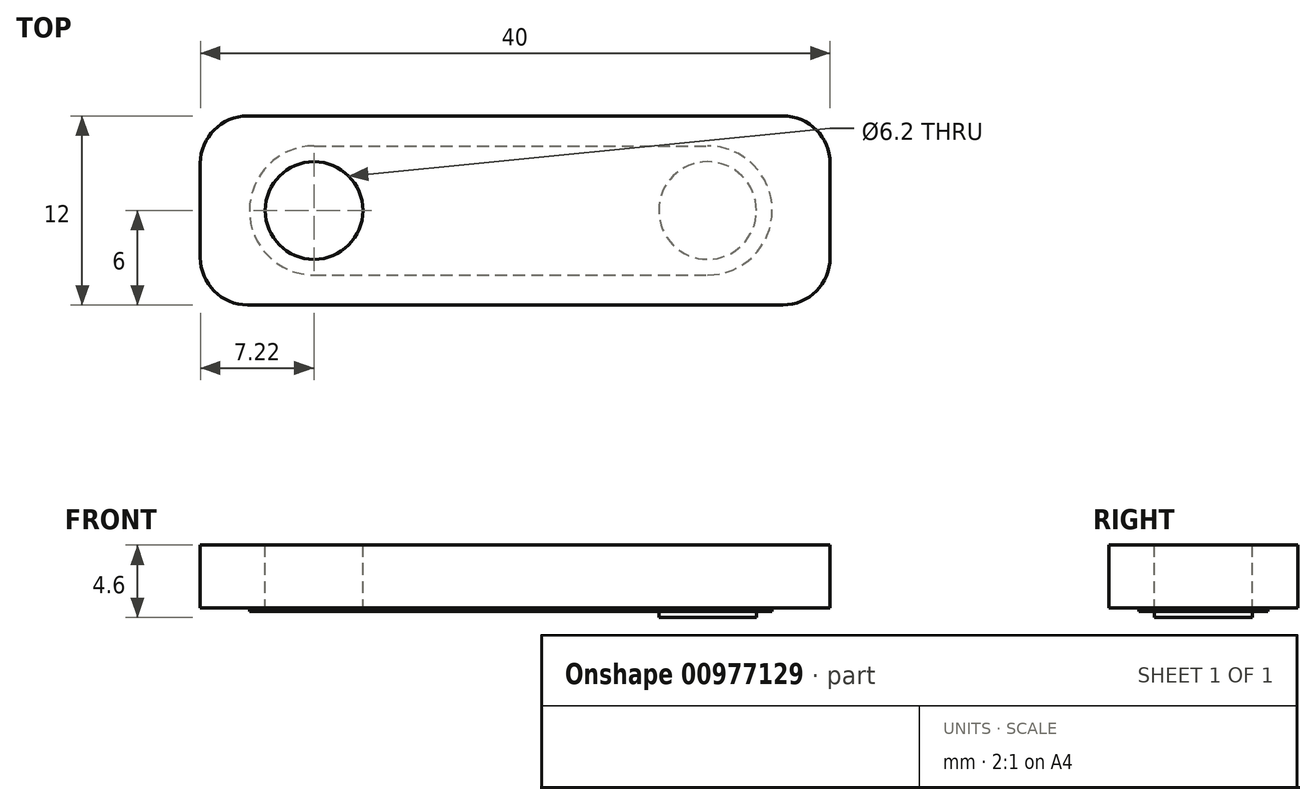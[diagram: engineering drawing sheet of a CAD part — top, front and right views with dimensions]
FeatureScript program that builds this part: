
annotation { "Feature Type Name" : "Feature", "Feature Type Description" : "" }
export const myFeature = defineFeature(function(context is Context, id is Id, definition is map)
    precondition{}
    {
        {
            var Q0;
            Q0=qCreatedBy(makeId("Top.planeOp"),FACE);
            var sketch = newSketch(context, id + "F0", { "sketchPlane" : qUnion([Q0])});
            skLineSegment(sketch, "E0.bottom", {"start": v(-7.22, 6) * mm, "end": v(32.78, 6) * mm});
            skLineSegment(sketch, "E0.top", {"start": v(-7.22, -6) * mm, "end": v(32.78, -6) * mm});
            skLineSegment(sketch, "E0.left", {"start": v(-7.22, 6) * mm, "end": v(-7.22, -6) * mm});
            skLineSegment(sketch, "E0.right", {"start": v(32.78, 6) * mm, "end": v(32.78, -6) * mm});
            skPoint(sketch, "E1", {"position": v(-7.22, 0) * mm});
            skPoint(sketch, "E2", {"position": v(0, 0) * mm});
            skSolve(sketch);
        }
        {
            var Q0;
            Q0=qCreatedBy(makeId("Top.planeOp"),FACE);
            var sketch = newSketch(context, id + "F1", { "sketchPlane" : qUnion([Q0])});
            skCircle(sketch, "E3", {"center": v(0, 0) * mm, "radius": 4.1 * mm});
            skCircle(sketch, "E4", {"center": v(25, 0) * mm, "radius": 4.1 * mm});
            skLineSegment(sketch, "E5", {"start": v(0, 4.1) * mm, "end": v(25, 4.1) * mm});
            skLineSegment(sketch, "E6", {"start": v(0, -4.1) * mm, "end": v(25, -4.1) * mm});
            skSolve(sketch);
        }
        {
            var Q0;
            Q0 = qSketchRegion(id + "F1", true);
            extrude(context, id + "F2", {"entities" : qUnion([Q0]), "depth" : -0.2 * mm, "offsetDistance" : 25 * mm});
        }
        {
            var Q0;
            Q0=qCreatedBy(makeId("Top.planeOp"),FACE);
            var sketch = newSketch(context, id + "F3", { "sketchPlane" : qUnion([Q0])});
            skCircle(sketch, "E7", {"center": v(25, 0) * mm, "radius": 3.1 * mm});
            skSolve(sketch);
        }
        {
            var Q0;
            Q0 = qSketchRegion(id + "F0", true);
            extrude(context, id + "F4", {"entities" : qUnion([Q0]), "operationType" : NewBodyOperationType.ADD, "depth" : 4 * mm, "offsetDistance" : 25 * mm});
        }
        {
            var Q0;
            Q0=makeQuery(id+"F4.opExtrude","SWEPT_EDGE",EDGE,{"disambiguationData":[OSD([sQuery(id+"F0.wireOp",EDGE,"E0.top"),sQuery(id+"F0.wireOp",EDGE,"E0.right")])]});
            var Q1;
            Q1=makeQuery(id+"F4.opExtrude","SWEPT_EDGE",EDGE,{"disambiguationData":[OSD([sQuery(id+"F0.wireOp",EDGE,"E0.bottom"),sQuery(id+"F0.wireOp",EDGE,"E0.right")])]});
            var Q2;
            Q2=makeQuery(id+"F4.opExtrude","SWEPT_EDGE",EDGE,{"disambiguationData":[OSD([sQuery(id+"F0.wireOp",EDGE,"E0.top"),sQuery(id+"F0.wireOp",EDGE,"E0.left")])]});
            var Q3;
            Q3=makeQuery(id+"F4.opExtrude","SWEPT_EDGE",EDGE,{"disambiguationData":[OSD([sQuery(id+"F0.wireOp",EDGE,"E0.bottom"),sQuery(id+"F0.wireOp",EDGE,"E0.left")])]});
            fillet(context, id + "F5", {"entities" : qUnion([Q0, Q1, Q2, Q3]), "radius" : 3 * mm, "tangentPropagation" : true, "allowEdgeOverflow" : false});
        }
        {
            var Q0;
            Q0=makeQuery(id+"F4.opExtrude","CAP_FACE",FACE,{"disambiguationData":[OSD([sQuery(id+"F0.wireOp",EDGE,"E0.bottom"),sQuery(id+"F0.wireOp",EDGE,"E0.top"),sQuery(id+"F0.wireOp",EDGE,"E0.left"),sQuery(id+"F0.wireOp",EDGE,"E0.right")])],"isStart":false});
            var sketch = newSketch(context, id + "F6", { "sketchPlane" : qUnion([Q0])});
            skPoint(sketch, "E8", {"position": v(0, 0) * mm});
            skSolve(sketch);
        }
        {
            var Q0;
            Q0=sQuery(id+"F6.wireOp",VERTEX,"E8");
            var Q1;
            Q1=makeQuery(id+"F2.opExtrude","SWEPT_BODY",BODY,{"disambiguationData":[OSD([sQuery(id+"F1.wireOp",EDGE,"E3"),sQuery(id+"F1.wireOp",EDGE,"E4"),sQuery(id+"F1.wireOp",EDGE,"E5"),sQuery(id+"F1.wireOp",EDGE,"E6")])]});
            hole(context, id + "F7", {"style" : HoleStyle.SIMPLE, "endStyle" : HoleEndStyle.THROUGH, "holeDiameter" : 6.2 * mm, "majorDiameter" : 5 * mm, "isTappedThrough" : true, "tappedDepth" : 12 * mm, "tapClearance" : 3, "locations" : qUnion([Q0]), "scope" : qUnion([Q1])});
        }
        {
            var Q0;
            Q0 = qSketchRegion(id + "F3", true);
            extrude(context, id + "F8", {"entities" : qUnion([Q0]), "operationType" : NewBodyOperationType.ADD, "depth" : -0.6 * mm, "offsetDistance" : 25 * mm});
        }
    });
